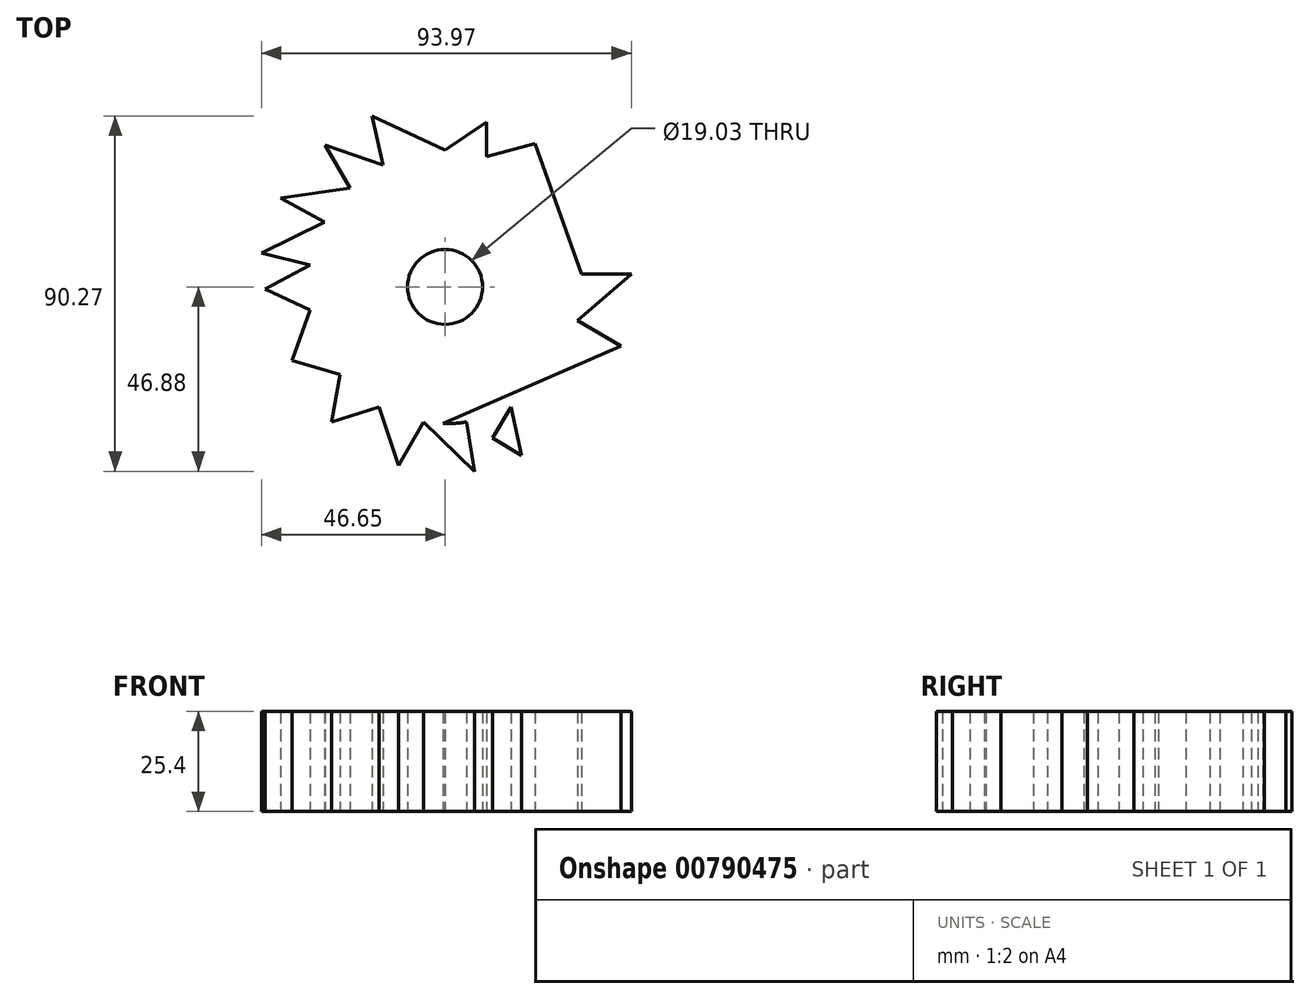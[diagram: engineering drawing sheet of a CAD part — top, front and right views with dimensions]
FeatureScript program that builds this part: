
annotation { "Feature Type Name" : "Feature", "Feature Type Description" : "" }
export const myFeature = defineFeature(function(context is Context, id is Id, definition is map)
    precondition{}
    {
        {
            var Q0;
            Q0=qCreatedBy(makeId("Top.planeOp"),FACE);
            var sketch = newSketch(context, id + "F0", { "sketchPlane" : qUnion([Q0])});
            skCircle(sketch, "E0", {"center": v(0, 0) * mm, "radius": 34.77 * mm});
            skLineSegment(sketch, "E1", {"start": v(0, 34.77) * mm, "end": v(0, 47.47) * mm});
            skLineSegment(sketch, "E2", {"start": v(0, 47.47) * mm, "end": v(0, 34.77) * mm});
            skLineSegment(sketch, "E3", {"start": v(0, 34.77) * mm, "end": v(10.55, 41.84) * mm});
            skLineSegment(sketch, "E4", {"start": v(10.55, 41.84) * mm, "end": v(10.55, 33.13) * mm});
            skLineSegment(sketch, "E5", {"start": v(10.55, 33.13) * mm, "end": v(22.84, 36.35) * mm});
            skLineSegment(sketch, "E6", {"start": v(22.84, 36.35) * mm, "end": v(34.62, 3.25) * mm});
            skLineSegment(sketch, "E7", {"start": v(34.62, 3.25) * mm, "end": v(47.32, 3.25) * mm});
            skLineSegment(sketch, "E8", {"start": v(47.32, 3.25) * mm, "end": v(33.71, -8.52) * mm});
            skLineSegment(sketch, "E9", {"start": v(33.71, -8.52) * mm, "end": v(44.64, -15) * mm});
            skLineSegment(sketch, "E10", {"start": v(44.64, -15) * mm, "end": v(-0.52, -34.77) * mm});
            skLineSegment(sketch, "E11", {"start": v(-0.52, -34.77) * mm, "end": v(10.55, -41) * mm});
            skLineSegment(sketch, "E12", {"start": v(10.55, -41) * mm, "end": v(16.74, -30.48) * mm});
            skLineSegment(sketch, "E13", {"start": v(16.74, -30.48) * mm, "end": v(19.42, -42.9) * mm});
            skLineSegment(sketch, "E14", {"start": v(19.42, -42.9) * mm, "end": v(5.5, -34.33) * mm});
            skLineSegment(sketch, "E15", {"start": v(5.5, -34.33) * mm, "end": v(7.45, -46.88) * mm});
            skLineSegment(sketch, "E16", {"start": v(7.45, -46.88) * mm, "end": v(-5.41, -34.35) * mm});
            skLineSegment(sketch, "E17", {"start": v(-5.41, -34.35) * mm, "end": v(-11.76, -45.34) * mm});
            skLineSegment(sketch, "E18", {"start": v(-11.76, -45.34) * mm, "end": v(-16.74, -30.48) * mm});
            skLineSegment(sketch, "E19", {"start": v(-16.74, -30.48) * mm, "end": v(-28.84, -34.34) * mm});
            skLineSegment(sketch, "E20", {"start": v(-28.84, -34.34) * mm, "end": v(-26.68, -22.3) * mm});
            skLineSegment(sketch, "E21", {"start": v(-26.68, -22.3) * mm, "end": v(-38.88, -18.77) * mm});
            skLineSegment(sketch, "E22", {"start": v(-38.88, -18.77) * mm, "end": v(-34.26, -5.93) * mm});
            skLineSegment(sketch, "E23", {"start": v(-34.26, -5.93) * mm, "end": v(-45.78, -0.59) * mm});
            skLineSegment(sketch, "E24", {"start": v(-45.78, -0.59) * mm, "end": v(-34.34, 5.48) * mm});
            skLineSegment(sketch, "E25", {"start": v(-34.34, 5.48) * mm, "end": v(-46.65, 8.6) * mm});
            skLineSegment(sketch, "E26", {"start": v(-46.65, 8.6) * mm, "end": v(-30.63, 16.46) * mm});
            skLineSegment(sketch, "E27", {"start": v(-30.63, 16.46) * mm, "end": v(-41.74, 22.61) * mm});
            skLineSegment(sketch, "E28", {"start": v(-41.74, 22.61) * mm, "end": v(-24.12, 25.04) * mm});
            skLineSegment(sketch, "E29", {"start": v(-24.12, 25.04) * mm, "end": v(-30.43, 36.07) * mm});
            skLineSegment(sketch, "E30", {"start": v(-30.43, 36.07) * mm, "end": v(-15.76, 31) * mm});
            skLineSegment(sketch, "E31", {"start": v(-15.76, 31) * mm, "end": v(-18.54, 43.39) * mm});
            skLineSegment(sketch, "E32", {"start": v(-18.54, 43.39) * mm, "end": v(0, 34.77) * mm});
            skCircle(sketch, "E33", {"center": v(0, 0) * mm, "radius": 9.51 * mm});
            skSolve(sketch);
        }
        {
            var Q0;
            Q0=makeQuery(id+"F0.imprint","IMPRINT",FACE,{"disambiguationData":[TD([[makeQuery(id+"F0.imprint","IMPRINT",EDGE,{"derivedFrom":sQuery(id+"F0.wireOp",EDGE,"E33")}),-1.0]])]});
            var Q1;
            {var subQ0=sQuery(id+"F0.wireOp",EDGE,"E23");Q1=makeQuery(id+"F0.imprint","IMPRINT",FACE,{"disambiguationData":[TD([[makeQuery(id+"F0.imprint","IMPRINT",EDGE,{"derivedFrom":subQ0}),-1.0]])]});}
            var Q2;
            {var subQ0=sQuery(id+"F0.wireOp",EDGE,"E21");Q2=makeQuery(id+"F0.imprint","IMPRINT",FACE,{"disambiguationData":[TD([[makeQuery(id+"F0.imprint","IMPRINT",EDGE,{"derivedFrom":subQ0}),-1.0]])]});}
            var Q3;
            {var subQ0=sQuery(id+"F0.wireOp",EDGE,"E19");Q3=makeQuery(id+"F0.imprint","IMPRINT",FACE,{"disambiguationData":[TD([[makeQuery(id+"F0.imprint","IMPRINT",EDGE,{"derivedFrom":subQ0}),-1.0]])]});}
            var Q4;
            {var subQ0=sQuery(id+"F0.wireOp",EDGE,"E17");Q4=makeQuery(id+"F0.imprint","IMPRINT",FACE,{"disambiguationData":[TD([[makeQuery(id+"F0.imprint","IMPRINT",EDGE,{"derivedFrom":subQ0}),-1.0]])]});}
            var Q5;
            {var subQ0=sQuery(id+"F0.wireOp",EDGE,"E15");Q5=makeQuery(id+"F0.imprint","IMPRINT",FACE,{"disambiguationData":[TD([[makeQuery(id+"F0.imprint","IMPRINT",EDGE,{"derivedFrom":subQ0}),-1.0]])]});}
            var Q6;
            {var subQ0=sQuery(id+"F0.wireOp",EDGE,"E13");Q6=makeQuery(id+"F0.imprint","IMPRINT",FACE,{"disambiguationData":[TD([[makeQuery(id+"F0.imprint","IMPRINT",EDGE,{"derivedFrom":subQ0}),-1.0]])]});}
            var Q7;
            {var subQ0=sQuery(id+"F0.wireOp",EDGE,"E11");Q7=makeQuery(id+"F0.imprint","IMPRINT",FACE,{"disambiguationData":[TD([[makeQuery(id+"F0.imprint","IMPRINT",EDGE,{"derivedFrom":subQ0}),-1.0]])]});}
            var Q8;
            {var subQ0=sQuery(id+"F0.wireOp",EDGE,"E9");Q8=makeQuery(id+"F0.imprint","IMPRINT",FACE,{"disambiguationData":[TD([[makeQuery(id+"F0.imprint","IMPRINT",EDGE,{"derivedFrom":subQ0}),-1.0]])]});}
            var Q9;
            {var subQ0=sQuery(id+"F0.wireOp",EDGE,"E7");Q9=makeQuery(id+"F0.imprint","IMPRINT",FACE,{"disambiguationData":[TD([[makeQuery(id+"F0.imprint","IMPRINT",EDGE,{"derivedFrom":subQ0}),-1.0]])]});}
            var Q10;
            {var subQ0=sQuery(id+"F0.wireOp",EDGE,"E5");Q10=makeQuery(id+"F0.imprint","IMPRINT",FACE,{"disambiguationData":[TD([[makeQuery(id+"F0.imprint","IMPRINT",EDGE,{"derivedFrom":subQ0}),-1.0]])]});}
            var Q11;
            {var subQ0=sQuery(id+"F0.wireOp",EDGE,"E3");Q11=makeQuery(id+"F0.imprint","IMPRINT",FACE,{"disambiguationData":[TD([[makeQuery(id+"F0.imprint","IMPRINT",EDGE,{"derivedFrom":subQ0}),-1.0]])]});}
            var Q12;
            {var subQ0=sQuery(id+"F0.wireOp",EDGE,"E1");Q12=makeQuery(id+"F0.imprint","IMPRINT",FACE,{"disambiguationData":[TD([[makeQuery(id+"F0.imprint","IMPRINT",EDGE,{"derivedFrom":subQ0}),-1.0]])]});}
            var Q13;
            {var subQ0=sQuery(id+"F0.wireOp",EDGE,"E1");Q13=makeQuery(id+"F0.imprint","IMPRINT",FACE,{"disambiguationData":[TD([[makeQuery(id+"F0.imprint","IMPRINT",EDGE,{"derivedFrom":subQ0}),-1.0]])]});}
            var Q14;
            {var subQ2=sQuery(id+"F0.wireOp",EDGE,"E31");Q14=makeQuery(id+"F0.imprint","IMPRINT",FACE,{"disambiguationData":[TD([[makeQuery(id+"F0.imprint","IMPRINT",EDGE,{"derivedFrom":subQ2}),-1.0]])]});}
            var Q15;
            {var subQ0=sQuery(id+"F0.wireOp",EDGE,"E29");Q15=makeQuery(id+"F0.imprint","IMPRINT",FACE,{"disambiguationData":[TD([[makeQuery(id+"F0.imprint","IMPRINT",EDGE,{"derivedFrom":subQ0}),-1.0]])]});}
            var Q16;
            {var subQ0=sQuery(id+"F0.wireOp",EDGE,"E27");Q16=makeQuery(id+"F0.imprint","IMPRINT",FACE,{"disambiguationData":[TD([[makeQuery(id+"F0.imprint","IMPRINT",EDGE,{"derivedFrom":subQ0}),-1.0]])]});}
            var Q17;
            {var subQ0=sQuery(id+"F0.wireOp",EDGE,"E25");Q17=makeQuery(id+"F0.imprint","IMPRINT",FACE,{"disambiguationData":[TD([[makeQuery(id+"F0.imprint","IMPRINT",EDGE,{"derivedFrom":subQ0}),-1.0]])]});}
            extrude(context, id + "F1", {"entities" : qUnion([Q0, Q1, Q2, Q3, Q4, Q5, Q6, Q7, Q8, Q9, Q10, Q11, Q12, Q13, Q14, Q15, Q16, Q17]), "depth" : 25.4 * mm, "offsetDistance" : 25.4 * mm});
        }
    });
